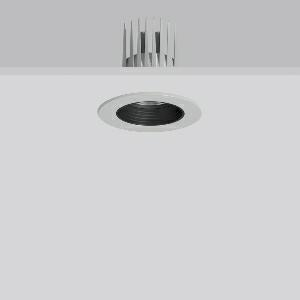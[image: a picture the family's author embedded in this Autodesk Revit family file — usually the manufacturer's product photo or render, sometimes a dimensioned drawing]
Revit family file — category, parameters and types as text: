
# Revit family: heledon_mini_e_901751_004_3_0895
name_source: partatom
category: Lighting Fixtures
units: mm (PartAtom-declared; Revit-internal decimal feet)

## family parameters
Cut with Voids When Loaded = No
Host = Face
Light Source = No
Part Type = Normal
Room Calculation Point = No
Round Connector Dimension = Use Diameter
Shared = No

## types (1)
- HELEDON mini E (1 x LED Modul 935, 3250 lm, 3500)
    Apparent Load = 29 VA
    Approval mark = CE
    CIE Flux Codes = 99 100 100 100 100
    Color Rendering = 92
    Color Temperature = 3500
    Default Elevation = 1800 mm
    Description = Series: HELEDON mini
Round recessed downlight. Housing: die-cast aluminium, powder-coated. Black plastic ring and recessed LED to prevent glare from the side. Optical assembly with lens made of plastic (polycarbonate) for the best homogeneous light distribution - can be changed without tools. Best colour rendering index Ra>90. Suitable for Recessed ceiling mounting. Installation without tools thanks to spring fastening system. Including separate LED converter with connecting cable 600 mm.High quality converter without flickering and stroboscopic effect. Through-wiring box (5 pole) available as accessory. The following accessories can be mounted without use of tools: interchangeable lenses, decorative glasses, honeycomb louvre, clear and frosted diffusers, white interchangeable plastic ring. 
Colour: silver
Diameter: 124 mm
Height: 3 mm
Cut-out diameter: 114 mm
Recess height: 170 mm
Luminaire: recess height: 120 mm
Lamp: LED
Socket: without socket
Colour temperature: 3500K
Colour rendering index (CRI): 92
System power: 29 W
Rated luminous flux: 3250 lm
Luminous efficiency: 112 lm/W
Control gear: Regulated power supply
Protection class: II
Type of protection: IP 20
    Height = 0 mm  [stored 0 ft]
    Lamp = 1 x LED Modul 935
    Lamp Light Flux = 3250 lm
    Lamp count = 1
    Length = 124 mm  [stored 0.406824 ft]
    Lifetime = 50000 h
    Luminous efficacy = 112 lm/W
    Manufacturer = RZB
    ModVariant = No
    Model = 901751.004.3
    Mounting Place = Ceiling
    Mounting Type = Recessed
    Number of Poles = 1
    OnlyDefault = Yes
    Power Factor = 1
    Product Name = HELEDON mini E
    Product group = Recessed downlights
    ProductGroupID = 402
    Protection Class = Protection class II
    Protection Degree = IP 20
    RLX_Detail_Level = 1
    RLX_Emergency_Light_Flux = 0 lm
    RLX_Emergency_Type = 0
    RLX_Emergency_Type_DB = No
    RlxData = <blob elided: 128989 chars, md5=6409217b>
    Socket = socket
    Standby Power = 0 W
    System Light Flux = 3250 lm
    System Power = 29 W
    Type Comments = Product without accessories
    Type Image = 901656.004.jpg
    URL = http://relux.com
    VarID = ---
    Voltage = 230 V
    Voltage Range = 220-240 V
    Weight = 0.00 kg
    Width = 0 mm  [stored 0 ft]

note: [stored X ft] marks values corroborated as IEEE doubles in the binary element streams (Revit-internal decimal feet)

## geometry (parser evidence)
native form markers: Blend x4, Sweep x10
no freeform markers — native parametric forms only
